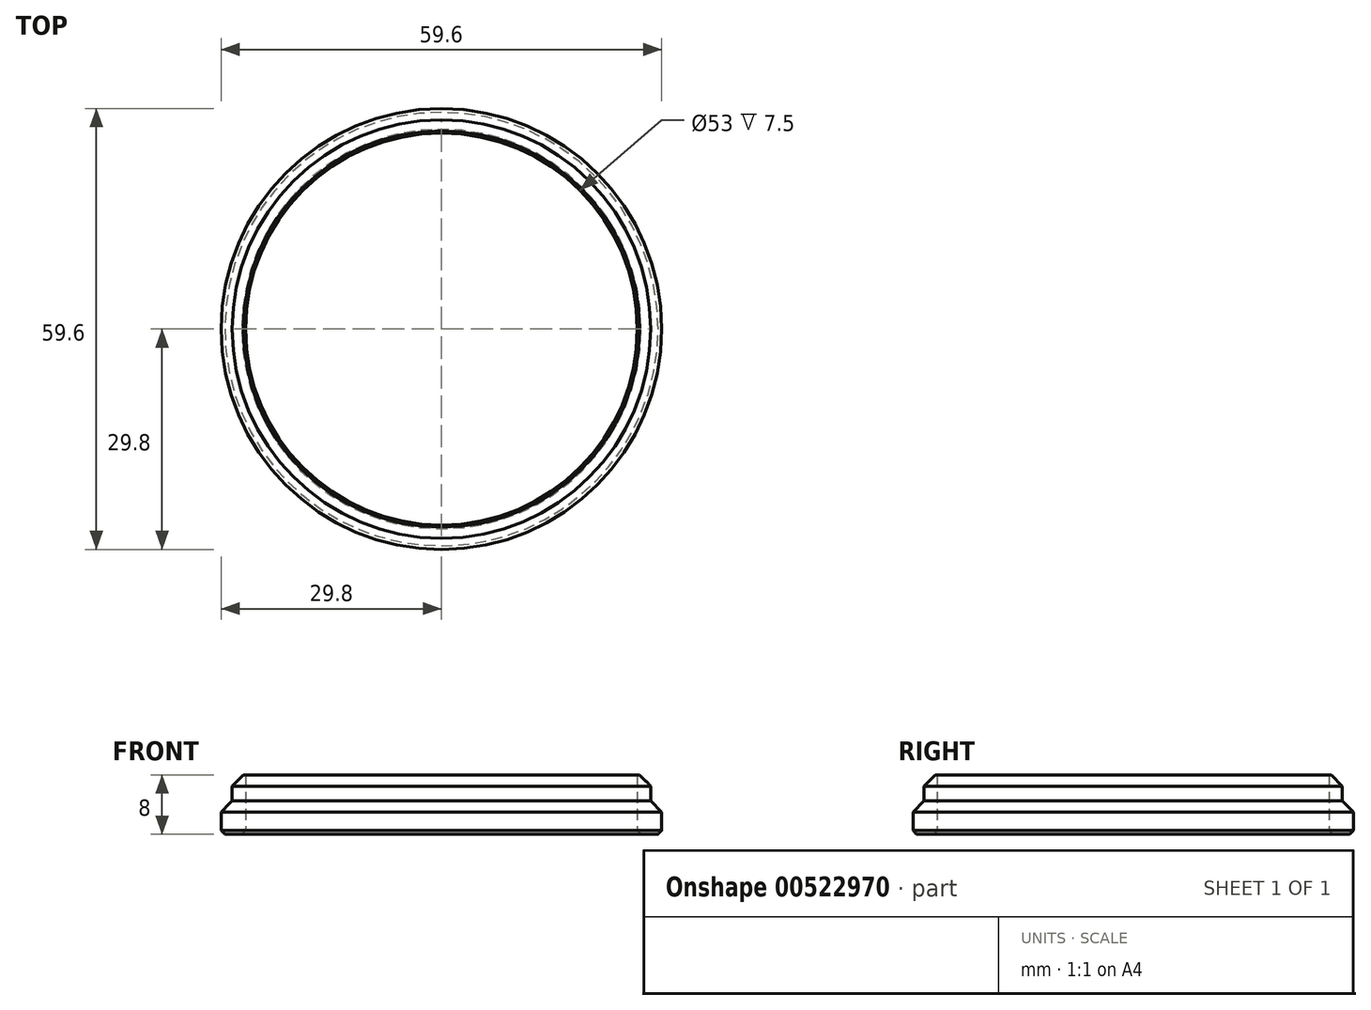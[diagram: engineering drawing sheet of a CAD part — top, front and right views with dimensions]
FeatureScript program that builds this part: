
annotation { "Feature Type Name" : "Feature", "Feature Type Description" : "" }
export const myFeature = defineFeature(function(context is Context, id is Id, definition is map)
    precondition{}
    {
        {
            var Q0;
            Q0=qCreatedBy(makeId("Top.planeOp"),FACE);
            var sketch = newSketch(context, id + "F0", { "sketchPlane" : qUnion([Q0])});
            skCircle(sketch, "E0", {"center": v(0, 0) * mm, "radius": 26.5 * mm});
            skCircle(sketch, "E1.0", {"center": v(0, 0) * mm, "radius": 28.3 * mm});
            skSolve(sketch);
        }
        {
            var Q0;
            Q0=makeQuery(id+"F0.imprint","IMPRINT",FACE,{"disambiguationData":[TD([[makeQuery(id+"F0.imprint","IMPRINT",EDGE,{"derivedFrom":sQuery(id+"F0.wireOp",EDGE,"E0")}),-1.0]])]});
            extrude(context, id + "F1", {"entities" : qUnion([Q0]), "depth" : 8 * mm, "offsetDistance" : 25 * mm});
        }
        {
            var Q0;
            Q0=makeQuery(id+"F1.opExtrude","CAP_EDGE",EDGE,{"disambiguationData":[OSD([sQuery(id+"F0.wireOp",EDGE,"E1.0")])],"isStart":false});
            chamfer(context, id + "F2", {"entities" : qUnion([Q0]), "width" : 1.5 * mm, "tangentPropagation" : true});
        }
        {
            var Q0;
            Q0=makeQuery(id+"F1.opExtrude","CAP_EDGE",EDGE,{"disambiguationData":[OSD([sQuery(id+"F0.wireOp",EDGE,"E0")])],"isStart":true});
            chamfer(context, id + "F3", {"entities" : qUnion([Q0]), "width" : .5 * mm, "tangentPropagation" : true});
        }
        {
            var Q0;
            Q0=makeQuery(id+"F1.opExtrude","CAP_FACE",FACE,{"disambiguationData":[OSD([sQuery(id+"F0.wireOp",EDGE,"E0"),sQuery(id+"F0.wireOp",EDGE,"E1.0")])],"isStart":true});
            var sketch = newSketch(context, id + "F4", { "sketchPlane" : qUnion([Q0])});
            skCircle(sketch, "E2.0", {"center": v(0, 0) * mm, "radius": 29.8 * mm});
            skSolve(sketch);
        }
        {
            var Q0;
            Q0=makeQuery(id+"F4.imprint","IMPRINT",FACE,{"disambiguationData":[TD([[makeQuery(id+"F4.imprint","IMPRINT",EDGE,{"derivedFrom":sQuery(id+"F4.wireOp",EDGE,"E2.0")}),1.0]])]});
            extrude(context, id + "F5", {"entities" : qUnion([Q0]), "operationType" : NewBodyOperationType.ADD, "oppositeDirection" : true, "depth" : 4.5 * mm, "offsetDistance" : 25 * mm});
        }
        {
            var Q0;
            Q0=makeQuery(id+"F5.opExtrude","CAP_EDGE",EDGE,{"disambiguationData":[OSD([sQuery(id+"F4.wireOp",EDGE,"E2.0")])],"isStart":false});
            chamfer(context, id + "F6", {"entities" : qUnion([Q0]), "width" : 1.5 * mm, "tangentPropagation" : true});
        }
        {
            var Q0;
            Q0=makeQuery(id+"F5.opExtrude","CAP_EDGE",EDGE,{"disambiguationData":[OSD([sQuery(id+"F4.wireOp",EDGE,"E2.0")])],"isStart":true});
            chamfer(context, id + "F7", {"entities" : qUnion([Q0]), "width" : .5 * mm});
        }
    });
